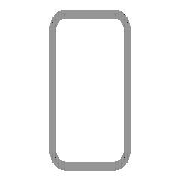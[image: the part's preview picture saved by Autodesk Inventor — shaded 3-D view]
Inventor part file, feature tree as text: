
AUTODESK INVENTOR PART (.ipt)
format: ipt  version: 2025 (Build 290162010, 162A)  size: 155,648 bytes
history: native  units: mm (DEFAULTED — no unit token found)
features: other x3, sketch x2, extrude x1, plane x1
ambient origin geometry x8: Origin, YZ Plane, XZ Plane, XY Plane, X Axis, Y Axis, Z Axis, Center Point
bodies: Solid1 (feature_tree), Body (feature_tree)
feature tree (7):
  other  "Driven Length"
  other  "Start plane"
  other  "End plane"
  extrude  "Extrusion3"  TaperAngle=0.0deg  [1 undecoded]
  sketch  "Sketch3"  dims[d3=4381.295mm d4=0.0mm]
  plane  "Work Plane3"
  sketch  "Sketch6"  dims[d7=4.0mm d9=20.0mm d11=40.0mm d12=2.0mm d13=-0.0mm d14=4381.295mm d15=10.0mm d16=20.0mm d17=90.0deg d18=4381.295mm d22=5.846853mm d23=0.0mm d24=0.0mm d28=9.86111mm]
note: 1 required parameter value undecoded (feature->parameter linkage not recoverable at this tier; creation-order binding heuristic only, values carry confidence <= 0.55)
